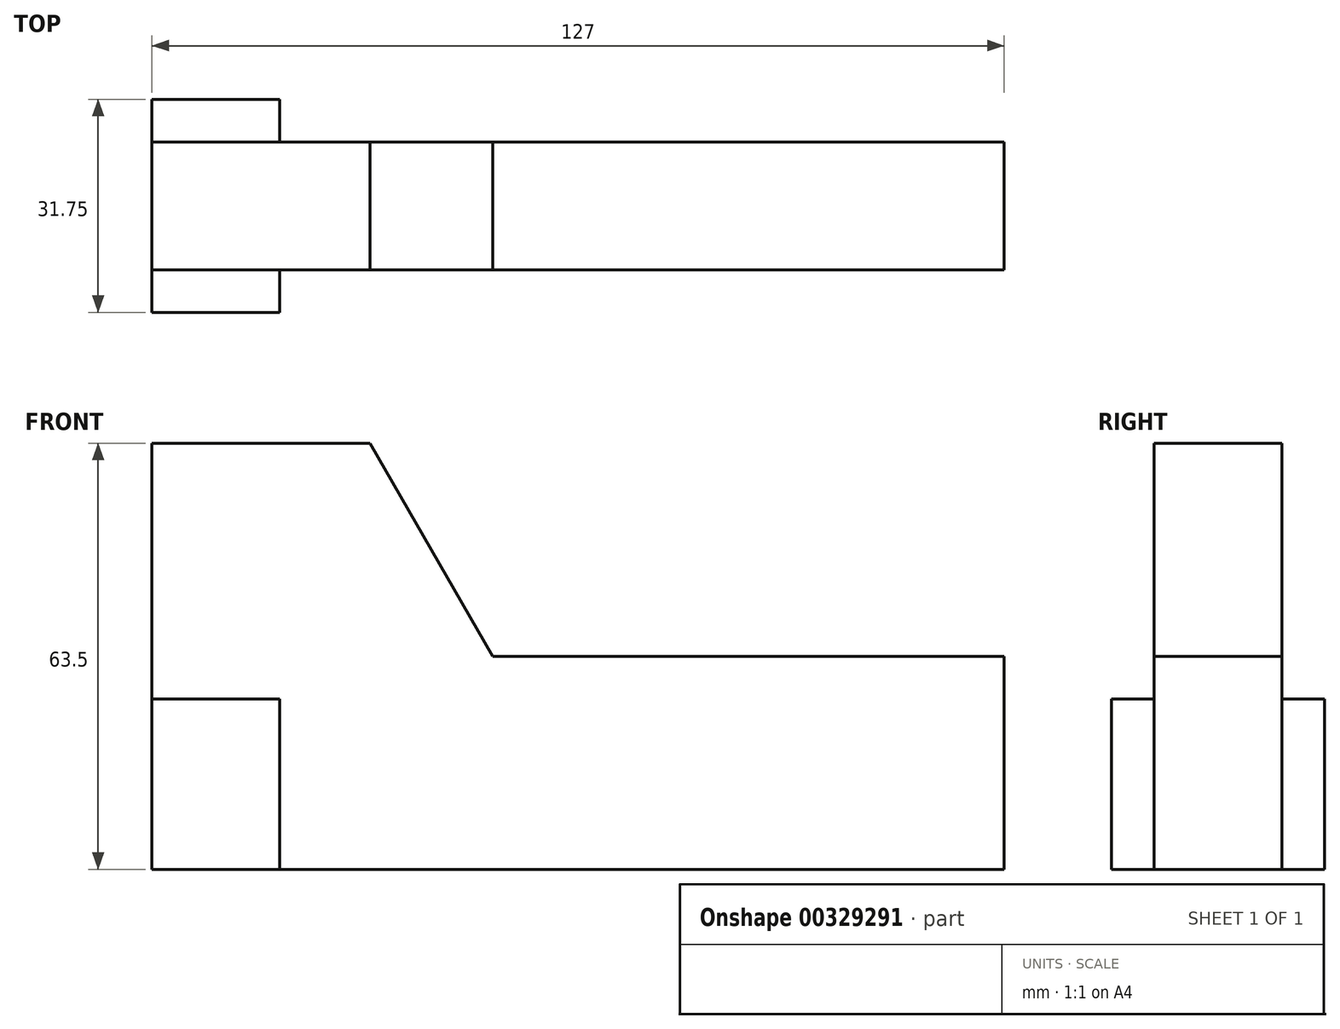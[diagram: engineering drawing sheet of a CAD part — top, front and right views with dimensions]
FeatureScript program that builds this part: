
annotation { "Feature Type Name" : "Feature", "Feature Type Description" : "" }
export const myFeature = defineFeature(function(context is Context, id is Id, definition is map)
    precondition{}
    {
        {
            var Q0;
            Q0=qCreatedBy(makeId("Front.planeOp"),FACE);
            var sketch = newSketch(context, id + "F0", { "sketchPlane" : qUnion([Q0])});
            skLineSegment(sketch, "E0", {"start": v(-75.02, -28.92) * mm, "end": v(51.98, -28.92) * mm});
            skLineSegment(sketch, "E1", {"start": v(51.98, -28.92) * mm, "end": v(51.98, 2.83) * mm});
            skLineSegment(sketch, "E2", {"start": v(-75.02, -28.92) * mm, "end": v(-75.02, 34.58) * mm});
            skLineSegment(sketch, "E3", {"start": v(51.98, 2.83) * mm, "end": v(-24.22, 2.83) * mm});
            skLineSegment(sketch, "E4", {"start": v(-75.02, 34.58) * mm, "end": v(-42.56, 34.58) * mm});
            skLineSegment(sketch, "E5", {"start": v(-42.56, 34.58) * mm, "end": v(-24.22, 2.83) * mm});
            skLineSegment(sketch, "E6", {"start": v(-55.97, -28.92) * mm, "end": v(-55.97, -3.52) * mm});
            skLineSegment(sketch, "E7", {"start": v(-55.97, -3.52) * mm, "end": v(-75.02, -3.52) * mm});
            skSolve(sketch);
        }
        {
            var Q0;
            {var subQ3=sQuery(id+"F0.wireOp",EDGE,"E1");Q0=makeQuery(id+"F0.imprint","IMPRINT",FACE,{"disambiguationData":[TD([[makeQuery(id+"F0.imprint","IMPRINT",EDGE,{"derivedFrom":subQ3}),1.0]])]});}
            extrude(context, id + "F1", {"entities" : qUnion([Q0]), "depth" : 19.05 * mm});
        }
        {
            var Q0;
            {var subQ3=sQuery(id+"F0.wireOp",EDGE,"E6");Q0=makeQuery(id+"F0.imprint","IMPRINT",FACE,{"disambiguationData":[TD([[makeQuery(id+"F0.imprint","IMPRINT",EDGE,{"derivedFrom":subQ3}),1.0]])]});}
            extrude(context, id + "F2", {"entities" : qUnion([Q0]), "operationType" : NewBodyOperationType.ADD, "depth" : 25.4 * mm});
        }
        {
            var Q0;
            {var subQ3=sQuery(id+"F0.wireOp",EDGE,"E6");Q0=makeQuery(id+"F0.imprint","IMPRINT",FACE,{"disambiguationData":[TD([[makeQuery(id+"F0.imprint","IMPRINT",EDGE,{"derivedFrom":subQ3}),1.0]])]});}
            extrude(context, id + "F3", {"entities" : qUnion([Q0]), "operationType" : NewBodyOperationType.ADD, "oppositeDirection" : true, "depth" : 6.35 * mm});
        }
    });
